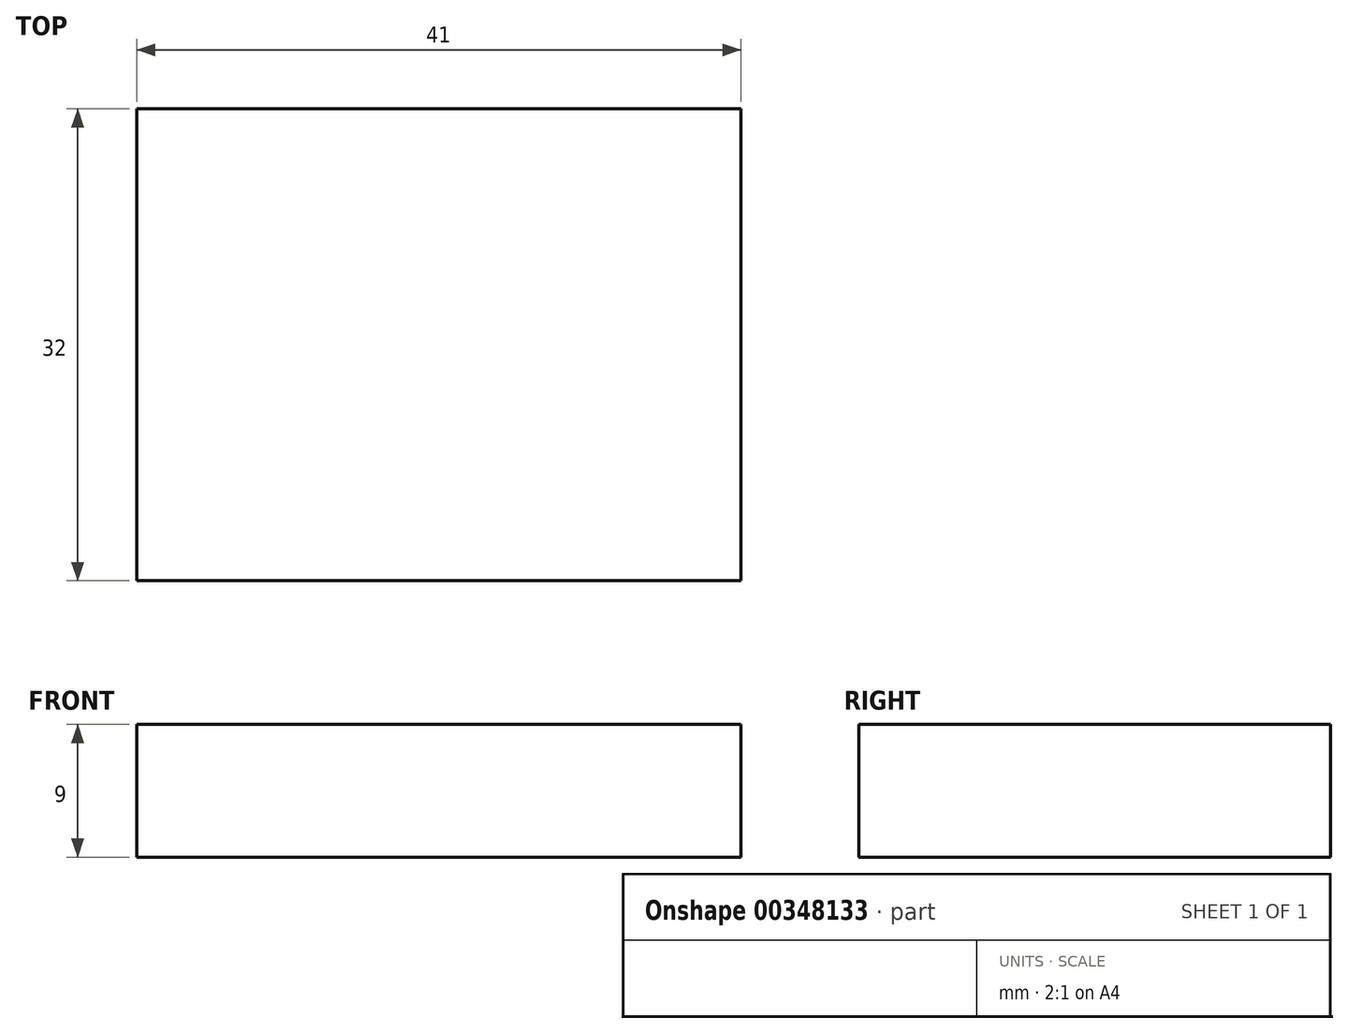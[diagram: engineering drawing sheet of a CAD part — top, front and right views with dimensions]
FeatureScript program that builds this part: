
annotation { "Feature Type Name" : "Feature", "Feature Type Description" : "" }
export const myFeature = defineFeature(function(context is Context, id is Id, definition is map)
    precondition{}
    {
        {
            var Q0;
            Q0=qCreatedBy(makeId("Top.planeOp"),FACE);
            var sketch = newSketch(context, id + "F0", { "sketchPlane" : qUnion([Q0])});
            skLineSegment(sketch, "E0.bottom", {"start": v(20.5, 16) * mm, "end": v(-20.5, 16) * mm});
            skLineSegment(sketch, "E0.top", {"start": v(20.5, -16) * mm, "end": v(-20.5, -16) * mm});
            skLineSegment(sketch, "E0.left", {"start": v(20.5, 16) * mm, "end": v(20.5, -16) * mm});
            skLineSegment(sketch, "E0.right", {"start": v(-20.5, 16) * mm, "end": v(-20.5, -16) * mm});
            skPoint(sketch, "E0.middle", {"position": v(0, 0) * mm});
            skSolve(sketch);
        }
        {
            var Q0;
            Q0=qCreatedBy(makeId("Front.planeOp"),FACE);
            var sketch = newSketch(context, id + "F1", { "sketchPlane" : qUnion([Q0])});
            skLineSegment(sketch, "E1", {"start": v(0, 0) * mm, "end": v(0, 9) * mm});
            skSolve(sketch);
        }
        {
            var Q0;
            Q0=makeQuery(id+"F0.imprint","IMPRINT",FACE,{"disambiguationData":[TD([[makeQuery(id+"F0.imprint","IMPRINT",EDGE,{"derivedFrom":sQuery(id+"F0.wireOp",EDGE,"E0.bottom")}),1.0]])]});
            var Q1;
            Q1=sQuery(id+"F1.wireOp",EDGE,"E1");
            sweep(context, id + "F2", {"profiles" : qUnion([Q0]), "path" : qUnion([Q1])});
        }
    });
